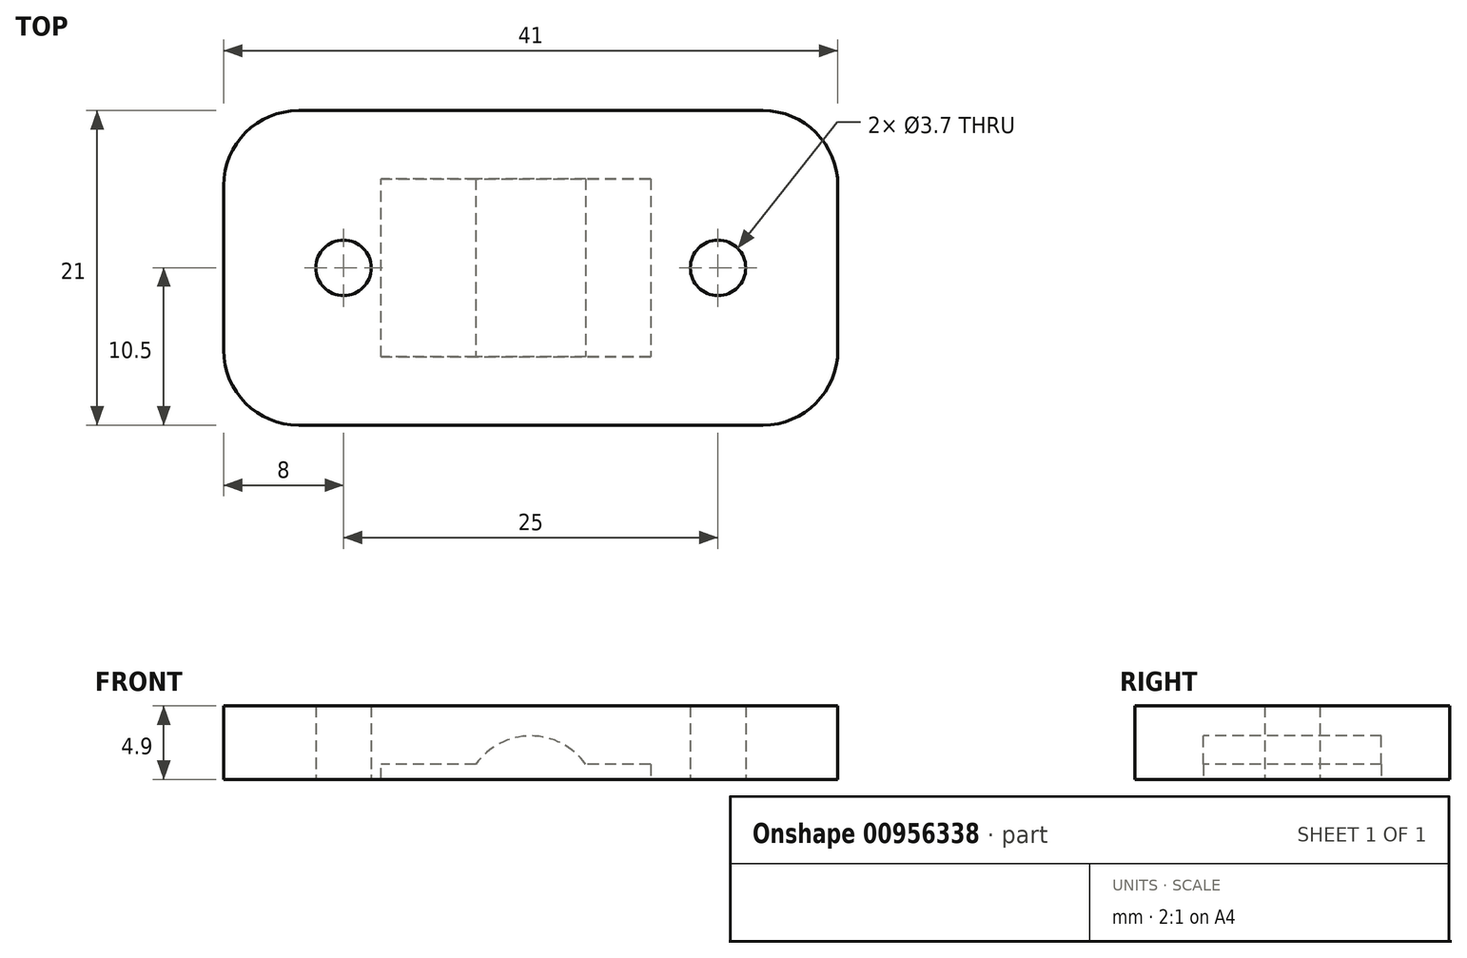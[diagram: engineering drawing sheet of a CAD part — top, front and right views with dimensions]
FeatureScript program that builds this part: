
annotation { "Feature Type Name" : "Feature", "Feature Type Description" : "" }
export const myFeature = defineFeature(function(context is Context, id is Id, definition is map)
    precondition{}
    {
        {
            assignVariable(context, id + "F0", {"name" : "tolerance_z", "anyValue" : 1});
        }
        {
            var Q0;
            Q0=qCreatedBy(makeId("Top.planeOp"),FACE);
            var sketch = newSketch(context, id + "F1", { "sketchPlane" : qUnion([Q0])});
            skLineSegment(sketch, "E0.bottom", {"start": v(15.5, 10.5) * mm, "end": v(-15.5, 10.5) * mm});
            skLineSegment(sketch, "E0.top", {"start": v(15.5, -10.5) * mm, "end": v(-15.5, -10.5) * mm});
            skLineSegment(sketch, "E0.left", {"start": v(20.5, 5.5) * mm, "end": v(20.5, -5.5) * mm});
            skLineSegment(sketch, "E0.right", {"start": v(-20.5, 5.5) * mm, "end": v(-20.5, -5.5) * mm});
            skPoint(sketch, "E0.middle", {"position": v(0, 0) * mm});
            skPoint(sketch, "E1.visualSharp", {"position": v(20.5, 10.5) * mm});
            skArc(sketch, "E1.filletArc", {"start": v(20.5, 5.5) * mm, "mid": v(19.04, 9.04) * mm, "end": v(15.5, 10.5) * mm});
            skPoint(sketch, "E2.visualSharp", {"position": v(20.5, -10.5) * mm});
            skArc(sketch, "E2.filletArc", {"start": v(15.5, -10.5) * mm, "mid": v(19.04, -9.04) * mm, "end": v(20.5, -5.5) * mm});
            skPoint(sketch, "E3.visualSharp", {"position": v(-20.5, -10.5) * mm});
            skArc(sketch, "E3.filletArc", {"start": v(-20.5, -5.5) * mm, "mid": v(-19.04, -9.04) * mm, "end": v(-15.5, -10.5) * mm});
            skPoint(sketch, "E4.visualSharp", {"position": v(-20.5, 10.5) * mm});
            skArc(sketch, "E4.filletArc", {"start": v(-15.5, 10.5) * mm, "mid": v(-19.04, 9.04) * mm, "end": v(-20.5, 5.5) * mm});
            skSolve(sketch);
        }
        {
            var Q0;
            Q0=makeQuery(id+"F1.imprint","IMPRINT",FACE,{"disambiguationData":[TD([[makeQuery(id+"F1.imprint","IMPRINT",EDGE,{"derivedFrom":sQuery(id+"F1.wireOp",EDGE,"E0.bottom")}),1.0]])]});
            extrude(context, id + "F2", {"entities" : qUnion([Q0]), "depth" : (6 + getVariable(context, 'tolerance_z') / 2) * mm, "offsetDistance" : 25 * mm, "hasSecondDirection" : true, "secondDirectionOppositeDirection" : true, "secondDirectionDepth" : -(1.1 + getVariable(context, 'tolerance_z') / 2) * mm});
        }
        {
            var Q0;
            Q0=qCreatedBy(makeId("Front.planeOp"),FACE);
            var sketch = newSketch(context, id + "F3", { "sketchPlane" : qUnion([Q0])});
            skCircle(sketch, "E5", {"center": v(0, 0) * mm, "radius": 4.5 * mm});
            skLineSegment(sketch, "E6.bottom", {"start": v(8, 2.6) * mm, "end": v(-8, 2.6) * mm});
            skLineSegment(sketch, "E6.top", {"start": v(8, -2.6) * mm, "end": v(-8, -2.6) * mm});
            skLineSegment(sketch, "E6.left", {"start": v(8, 2.6) * mm, "end": v(8, -2.6) * mm});
            skLineSegment(sketch, "E6.right", {"start": v(-8, 2.6) * mm, "end": v(-8, -2.6) * mm});
            skLineSegment(sketch, "E7.bottom", {"start": v(-8, -2.6) * mm, "end": v(-10, -2.6) * mm});
            skLineSegment(sketch, "E7.top", {"start": v(-8, 2.6) * mm, "end": v(-10, 2.6) * mm});
            skLineSegment(sketch, "E7.left", {"start": v(-8, -2.6) * mm, "end": v(-8, 2.6) * mm});
            skLineSegment(sketch, "E7.right", {"start": v(-10, -2.6) * mm, "end": v(-10, 2.6) * mm});
            skSolve(sketch);
        }
        {
            var Q0;
            Q0=qSketchRegion(id+"F3",true);
            extrude(context, id + "F4", {"entities" : qUnion([Q0]), "operationType" : NewBodyOperationType.REMOVE, "endBound" : BoundingType.SYMMETRIC, "oppositeDirection" : true, "depth" : 11.9 * mm, "offsetDistance" : 25 * mm});
        }
        {
            var Q0;
            Q0=qCreatedBy(makeId("Front.planeOp"),FACE);
            var sketch = newSketch(context, id + "F5", { "sketchPlane" : qUnion([Q0])});
            skLineSegment(sketch, "E8.bottom", {"start": v(-6.5, -1.5) * mm, "end": v(6.5, -1.5) * mm});
            skLineSegment(sketch, "E8.top", {"start": v(-6.5, 1.5) * mm, "end": v(6.5, 1.5) * mm});
            skLineSegment(sketch, "E8.left", {"start": v(-6.5, -1.5) * mm, "end": v(-6.5, 1.5) * mm});
            skLineSegment(sketch, "E8.right", {"start": v(6.5, -1.5) * mm, "end": v(6.5, 1.5) * mm});
            skPoint(sketch, "E8.middle", {"position": v(0, 0) * mm});
            skSolve(sketch);
        }
        {
            var Q0;
            Q0=makeQuery(id+"F5.imprint","IMPRINT",FACE,{"disambiguationData":[TD([[makeQuery(id+"F5.imprint","IMPRINT",EDGE,{"derivedFrom":sQuery(id+"F5.wireOp",EDGE,"E8.bottom")}),1.0]])]});
            extrude(context, id + "F6", {"entities" : qUnion([Q0]), "operationType" : NewBodyOperationType.REMOVE, "endBound" : BoundingType.SYMMETRIC, "oppositeDirection" : true, "depth" : 25 * mm, "offsetDistance" : 25 * mm});
        }
        {
            var Q0;
            {var subQ0=sQuery(id+"F1.wireOp",EDGE,"E1.filletArc");var subQ6=sQuery(id+"F1.wireOp",EDGE,"E0.left");var subQ7=sQuery(id+"F1.wireOp",EDGE,"E0.top");var subQ8=sQuery(id+"F1.wireOp",EDGE,"E0.bottom");var subQ9=sQuery(id+"F1.wireOp",EDGE,"E2.filletArc");Q0=makeQuery(id+"F6.boolean.opBoolean","SPLIT",FACE,{"disambiguationData":[TD([makeQuery(id+"F2.opExtrude","SWEPT_FACE",FACE,{"disambiguationData":[OSD([subQ6])]})])],"derivedFrom":makeQuery(id+"F2.opExtrude","CAP_FACE",FACE,{"disambiguationData":[OSD([subQ8,subQ7,subQ6,sQuery(id+"F1.wireOp",EDGE,"E0.right"),subQ0,subQ9,sQuery(id+"F1.wireOp",EDGE,"E3.filletArc"),sQuery(id+"F1.wireOp",EDGE,"E4.filletArc")])],"isStart":true})});}
            var sketch = newSketch(context, id + "F7", { "sketchPlane" : qUnion([Q0])});
            skCircle(sketch, "E9", {"center": v(-12.5, 0) * mm, "radius": 1.85 * mm});
            skCircle(sketch, "E10", {"center": v(12.5, 0) * mm, "radius": 1.85 * mm});
            skSolve(sketch);
        }
        {
            var Q0;
            Q0=makeQuery(id+"F7.imprint","IMPRINT",FACE,{"disambiguationData":[TD([[makeQuery(id+"F7.imprint","IMPRINT",EDGE,{"derivedFrom":sQuery(id+"F7.wireOp",EDGE,"E9")}),1.0]])]});
            var Q1;
            Q1=makeQuery(id+"F7.imprint","IMPRINT",FACE,{"disambiguationData":[TD([[makeQuery(id+"F7.imprint","IMPRINT",EDGE,{"derivedFrom":sQuery(id+"F7.wireOp",EDGE,"E10")}),1.0]])]});
            extrude(context, id + "F8", {"entities" : qUnion([Q0, Q1]), "operationType" : NewBodyOperationType.REMOVE, "oppositeDirection" : true, "depth" : 6 * mm, "offsetDistance" : 25 * mm});
        }
    });
